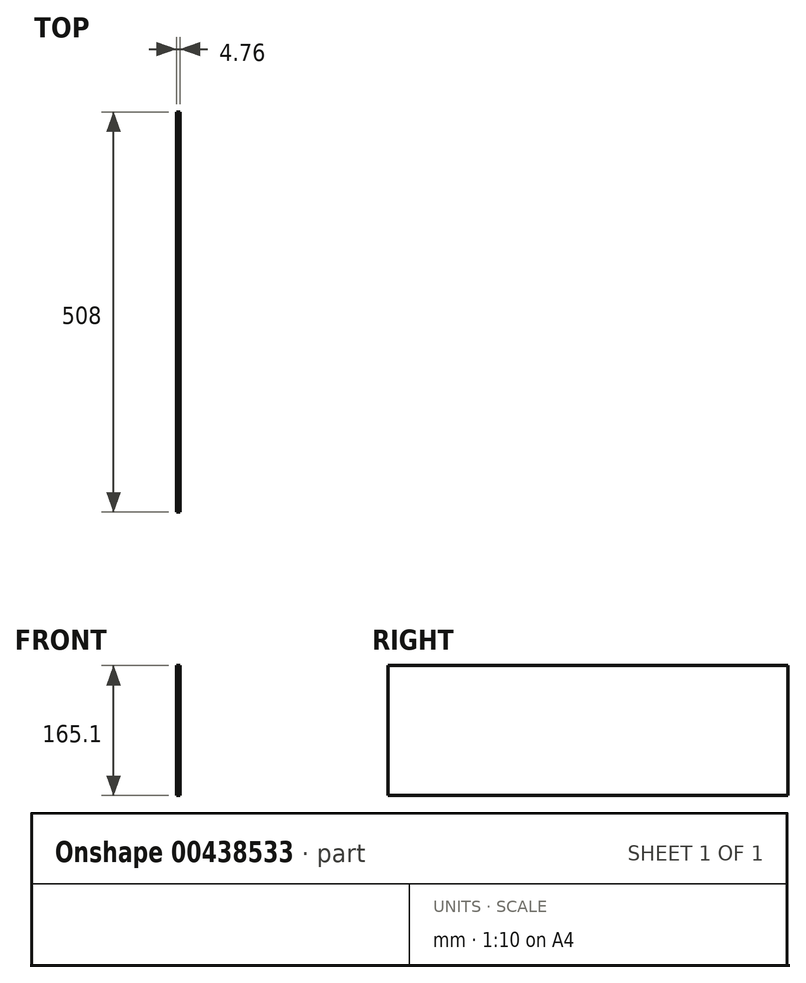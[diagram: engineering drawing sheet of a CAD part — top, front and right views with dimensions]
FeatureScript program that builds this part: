
annotation { "Feature Type Name" : "Feature", "Feature Type Description" : "" }
export const myFeature = defineFeature(function(context is Context, id is Id, definition is map)
    precondition{}
    {
        {
            var Q0;
            Q0=qCreatedBy(makeId("Right.planeOp"),FACE);
            var sketch = newSketch(context, id + "F0", { "sketchPlane" : qUnion([Q0])});
            skLineSegment(sketch, "E0.bottom", {"start": v(-138.58, 63.67) * mm, "end": v(369.42, 63.67) * mm});
            skLineSegment(sketch, "E0.top", {"start": v(-138.58, -101.43) * mm, "end": v(369.42, -101.43) * mm});
            skLineSegment(sketch, "E0.left", {"start": v(-138.58, 63.67) * mm, "end": v(-138.58, -101.43) * mm});
            skLineSegment(sketch, "E0.right", {"start": v(369.42, 63.67) * mm, "end": v(369.42, -101.43) * mm});
            skSolve(sketch);
        }
        {
            var Q0;
            Q0=makeQuery(id+"F0.imprint","IMPRINT",FACE,{"disambiguationData":[TD([[makeQuery(id+"F0.imprint","IMPRINT",EDGE,{"derivedFrom":sQuery(id+"F0.wireOp",EDGE,"E0.bottom")}),-1.0]])]});
            extrude(context, id + "F1", {"entities" : qUnion([Q0]), "depth" : 4.76 * mm});
        }
    });
